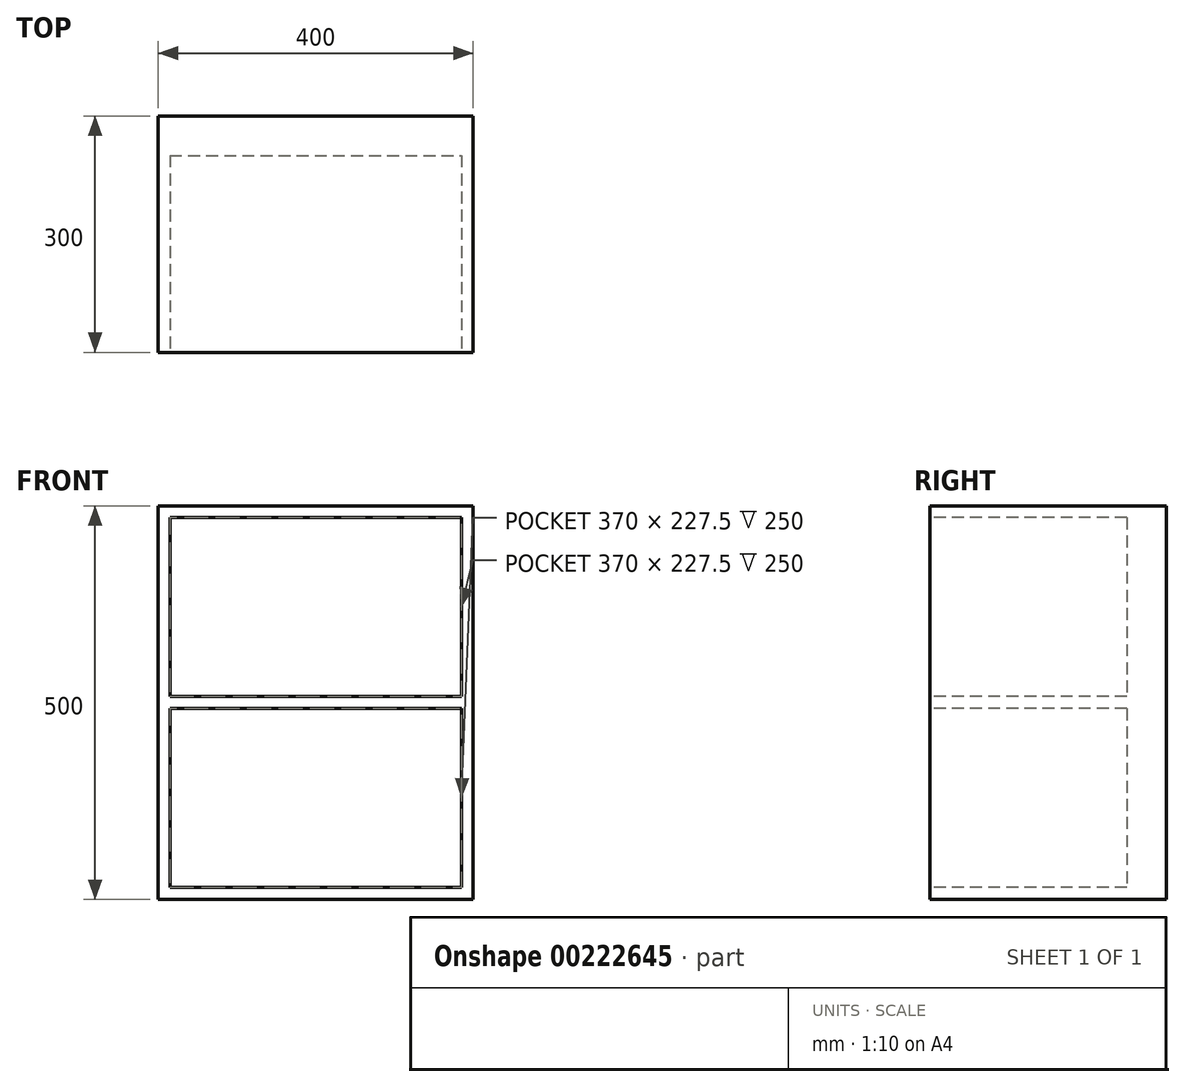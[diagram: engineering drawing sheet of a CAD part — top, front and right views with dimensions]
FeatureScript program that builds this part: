
annotation { "Feature Type Name" : "Feature", "Feature Type Description" : "" }
export const myFeature = defineFeature(function(context is Context, id is Id, definition is map)
    precondition{}
    {
        {
            var Q0;
            Q0=qCreatedBy(makeId("Front.planeOp"),FACE);
            var sketch = newSketch(context, id + "F0", { "sketchPlane" : qUnion([Q0])});
            skLineSegment(sketch, "E0.bottom", {"start": v(200, 250) * mm, "end": v(-200, 250) * mm});
            skLineSegment(sketch, "E0.top", {"start": v(200, -250) * mm, "end": v(-200, -250) * mm});
            skLineSegment(sketch, "E0.left", {"start": v(200, 250) * mm, "end": v(200, -250) * mm});
            skLineSegment(sketch, "E0.right", {"start": v(-200, 250) * mm, "end": v(-200, -250) * mm});
            skPoint(sketch, "E0.middle", {"position": v(0, 0) * mm});
            skSolve(sketch);
        }
        {
            var Q0;
            Q0=makeQuery(id+"F0.imprint","IMPRINT",FACE,{"disambiguationData":[TD([[makeQuery(id+"F0.imprint","IMPRINT",EDGE,{"derivedFrom":sQuery(id+"F0.wireOp",EDGE,"E0.bottom")}),1.0]])]});
            extrude(context, id + "F1", {"entities" : qUnion([Q0]), "depth" : 300 * mm});
        }
        {
            var Q0;
            Q0=makeQuery(id+"F1.opExtrude","CAP_FACE",FACE,{"disambiguationData":[OSD([sQuery(id+"F0.wireOp",EDGE,"E0.bottom"),sQuery(id+"F0.wireOp",EDGE,"E0.top"),sQuery(id+"F0.wireOp",EDGE,"E0.left"),sQuery(id+"F0.wireOp",EDGE,"E0.right")])],"isStart":false});
            var sketch = newSketch(context, id + "F2", { "sketchPlane" : qUnion([Q0])});
            skLineSegment(sketch, "E1.bottom", {"start": v(-185, 235) * mm, "end": v(185, 235) * mm});
            skLineSegment(sketch, "E1.top", {"start": v(-185, 7.5) * mm, "end": v(185, 7.5) * mm});
            skLineSegment(sketch, "E1.left", {"start": v(-185, 235) * mm, "end": v(-185, 7.5) * mm});
            skLineSegment(sketch, "E1.right", {"start": v(185, 235) * mm, "end": v(185, 7.5) * mm});
            skPoint(sketch, "E1.middle", {"position": v(0, 121.25) * mm});
            skLineSegment(sketch, "E2.bottom", {"start": v(-185, -7.5) * mm, "end": v(185, -7.5) * mm});
            skLineSegment(sketch, "E2.top", {"start": v(-185, -235) * mm, "end": v(185, -235) * mm});
            skLineSegment(sketch, "E2.left", {"start": v(-185, -7.5) * mm, "end": v(-185, -235) * mm});
            skLineSegment(sketch, "E2.right", {"start": v(185, -7.5) * mm, "end": v(185, -235) * mm});
            skPoint(sketch, "E2.middle", {"position": v(0, -121.25) * mm});
            skSolve(sketch);
        }
        {
            var Q0;
            Q0=makeQuery(id+"F2.imprint","IMPRINT",FACE,{"disambiguationData":[TD([[makeQuery(id+"F2.imprint","IMPRINT",EDGE,{"derivedFrom":sQuery(id+"F2.wireOp",EDGE,"E1.bottom")}),-1.0]])]});
            var Q1;
            Q1=makeQuery(id+"F2.imprint","IMPRINT",FACE,{"disambiguationData":[TD([[makeQuery(id+"F2.imprint","IMPRINT",EDGE,{"derivedFrom":sQuery(id+"F2.wireOp",EDGE,"E2.bottom")}),-1.0]])]});
            extrude(context, id + "F3", {"entities" : qUnion([Q0, Q1]), "operationType" : NewBodyOperationType.REMOVE, "oppositeDirection" : true, "depth" : 250 * mm});
        }
    });
